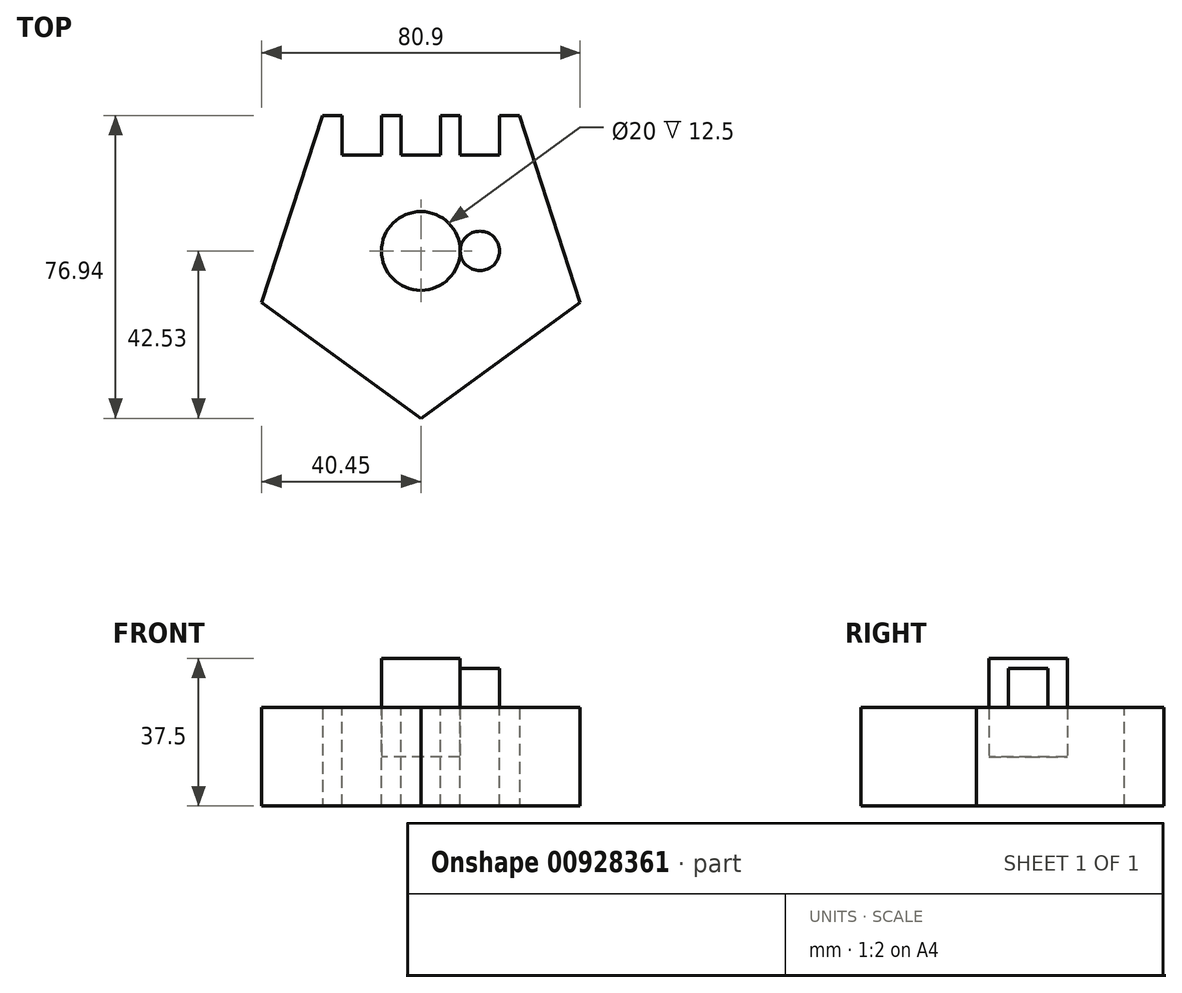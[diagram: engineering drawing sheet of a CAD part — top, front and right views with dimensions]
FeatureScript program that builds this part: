
annotation { "Feature Type Name" : "Feature", "Feature Type Description" : "" }
export const myFeature = defineFeature(function(context is Context, id is Id, definition is map)
    precondition{}
    {
        {
            var Q0;
            Q0=qCreatedBy(makeId("Top.planeOp"),FACE);
            var sketch = newSketch(context, id + "F0", { "sketchPlane" : qUnion([Q0])});
            skCircle(sketch, "E0.cCircle", {"center": v(0, 0) * mm, "radius": 34.4 * mm, "construction": true});
            skLineSegment(sketch, "E0.0", {"start": v(-40.45, -13.14) * mm, "end": v(-25, 34.4) * mm});
            skLineSegment(sketch, "E0.1", {"start": v(-25, 34.4) * mm, "end": v(25, 34.4) * mm});
            skLineSegment(sketch, "E0.2", {"start": v(25, 34.4) * mm, "end": v(40.45, -13.14) * mm});
            skLineSegment(sketch, "E0.3", {"start": v(40.45, -13.14) * mm, "end": v(0, -42.53) * mm});
            skLineSegment(sketch, "E0.4", {"start": v(0, -42.53) * mm, "end": v(-40.45, -13.14) * mm});
            skPoint(sketch, "E0.0.midPoint", {"position": v(-32.73, 10.63) * mm});
            skSolve(sketch);
        }
        {
            var Q0;
            Q0 = qSketchRegion(id + "F0", true);
            extrude(context, id + "F1", {"entities" : qUnion([Q0]), "depth" : 25 * mm, "offsetDistance" : 25 * mm});
        }
        {
            var Q0;
            Q0=makeQuery(id+"F1.opExtrude","CAP_FACE",FACE,{"disambiguationData":[OSD([sQuery(id+"F0.wireOp",EDGE,"E0.0"),sQuery(id+"F0.wireOp",EDGE,"E0.1"),sQuery(id+"F0.wireOp",EDGE,"E0.2"),sQuery(id+"F0.wireOp",EDGE,"E0.3"),sQuery(id+"F0.wireOp",EDGE,"E0.4")])],"isStart":false});
            var sketch = newSketch(context, id + "F2", { "sketchPlane" : qUnion([Q0])});
            skLineSegment(sketch, "E1", {"start": v(-20, 34.4) * mm, "end": v(-20, 24.4) * mm});
            skLineSegment(sketch, "E2", {"start": v(-20, 24.4) * mm, "end": v(-10, 24.4) * mm});
            skLineSegment(sketch, "E3", {"start": v(-10, 24.4) * mm, "end": v(-10, 34.4) * mm});
            skLineSegment(sketch, "E4.1.0.0", {"start": v(-5, 34.4) * mm, "end": v(-5, 24.4) * mm});
            skLineSegment(sketch, "E4.1.0.1", {"start": v(-5, 24.4) * mm, "end": v(5, 24.4) * mm});
            skLineSegment(sketch, "E4.1.0.2", {"start": v(5, 24.4) * mm, "end": v(5, 34.4) * mm});
            skLineSegment(sketch, "E4.2.0.0", {"start": v(10, 34.4) * mm, "end": v(10, 24.4) * mm});
            skLineSegment(sketch, "E4.2.0.1", {"start": v(10, 24.4) * mm, "end": v(20, 24.4) * mm});
            skLineSegment(sketch, "E4.2.0.2", {"start": v(20, 24.4) * mm, "end": v(20, 34.4) * mm});
            skLineSegment(sketch, "E4.direction1", {"start": v(-20, 24.4) * mm, "end": v(-5, 24.4) * mm, "construction": true});
            skLineSegment(sketch, "E5", {"start": v(-20, 34.4) * mm, "end": v(-10, 34.4) * mm});
            skLineSegment(sketch, "E6", {"start": v(-5, 34.4) * mm, "end": v(5, 34.4) * mm});
            skLineSegment(sketch, "E7", {"start": v(10, 34.4) * mm, "end": v(20, 34.4) * mm});
            skSolve(sketch);
        }
        {
            var Q0;
            Q0 = qSketchRegion(id + "F2", true);
            var Q1;
            Q1=makeQuery(id+"F1.opExtrude","CAP_FACE",FACE,{"disambiguationData":[OSD([sQuery(id+"F0.wireOp",EDGE,"E0.0"),sQuery(id+"F0.wireOp",EDGE,"E0.1"),sQuery(id+"F0.wireOp",EDGE,"E0.2"),sQuery(id+"F0.wireOp",EDGE,"E0.3"),sQuery(id+"F0.wireOp",EDGE,"E0.4")])],"isStart":true});
            extrude(context, id + "F3", {"entities" : qUnion([Q0]), "operationType" : NewBodyOperationType.REMOVE, "endBound" : BoundingType.UP_TO_SURFACE, "oppositeDirection" : true, "depth" : 25 * mm, "endBoundEntityFace" : qUnion([Q1]), "offsetDistance" : 25 * mm});
        }
        {
            var Q0;
            Q0=makeQuery(id+"F1.opExtrude","CAP_FACE",FACE,{"disambiguationData":[OSD([sQuery(id+"F0.wireOp",EDGE,"E0.0"),sQuery(id+"F0.wireOp",EDGE,"E0.1"),sQuery(id+"F0.wireOp",EDGE,"E0.2"),sQuery(id+"F0.wireOp",EDGE,"E0.3"),sQuery(id+"F0.wireOp",EDGE,"E0.4")])],"isStart":false});
            var sketch = newSketch(context, id + "F4", { "sketchPlane" : qUnion([Q0])});
            skCircle(sketch, "E8", {"center": v(0, 0) * mm, "radius": 10 * mm});
            skSolve(sketch);
        }
        {
            var Q0;
            Q0 = qSketchRegion(id + "F4", true);
            extrude(context, id + "F5", {"entities" : qUnion([Q0]), "endBound" : BoundingType.SYMMETRIC, "depth" : 25 * mm, "offsetDistance" : 25 * mm});
        }
        {
            var Q0;
            Q0=makeQuery(id+"F5.opExtrude","SWEPT_BODY",BODY,{"disambiguationData":[OSD([sQuery(id+"F4.wireOp",EDGE,"E8")])]});
            var Q1;
            Q1=makeQuery(id+"F1.opExtrude","SWEPT_BODY",BODY,{"disambiguationData":[OSD([sQuery(id+"F0.wireOp",EDGE,"E0.0"),sQuery(id+"F0.wireOp",EDGE,"E0.1"),sQuery(id+"F0.wireOp",EDGE,"E0.2"),sQuery(id+"F0.wireOp",EDGE,"E0.3"),sQuery(id+"F0.wireOp",EDGE,"E0.4")])]});
            booleanBodies(context, id + "F6", {"operationType" : BooleanOperationType.SUBTRACTION, "tools" : qUnion([Q0]), "targets" : qUnion([Q1]), "keepTools" : true});
        }
        {
            var Q0;
            Q0=makeQuery(id+"F1.opExtrude","CAP_FACE",FACE,{"disambiguationData":[OSD([sQuery(id+"F0.wireOp",EDGE,"E0.0"),sQuery(id+"F0.wireOp",EDGE,"E0.1"),sQuery(id+"F0.wireOp",EDGE,"E0.2"),sQuery(id+"F0.wireOp",EDGE,"E0.3"),sQuery(id+"F0.wireOp",EDGE,"E0.4")])],"isStart":false});
            var sketch = newSketch(context, id + "F7", { "sketchPlane" : qUnion([Q0])});
            skCircle(sketch, "E9", {"center": v(15, 0) * mm, "radius": 5 * mm});
            skSolve(sketch);
        }
        {
            var Q0;
            Q0 = qSketchRegion(id + "F7", true);
            extrude(context, id + "F8", {"entities" : qUnion([Q0]), "depth" : 10 * mm, "offsetDistance" : 25 * mm});
        }
    });
